# Revit family: ECDFPW314C
name_source: partatom
category: Plumbing Fixtures
units: mm (PartAtom-declared; Revit-internal decimal feet)

## family parameters
Always vertical = Yes
Cut with Voids When Loaded = No
OmniClass Number = 23.45.00.00
OmniClass Title = Sanitary, Laundry, and Cleaning Equipment
Part Type = Normal
Room Calculation Point = No
Round Connector Dimension = Use Diameter
Shared = Yes
Work Plane-Based = No

## types (1)
- ECDFPW314C
    Activation by = Mechanical Front Bubbler Button
    Approx. Shipping Weigh = 26 lbs
    Assembly Code = D2010810
    Bubbler Style = Flexi-Guard ® Safety Bubbler
    CW Connection = Yes
    Chilling Option = Non-refrigerated
    Description = Elkay Slimline Soft Sides Fountain Non-Filtered Non-Refrigerated
Stainless
    Dimensions (L x W x H) = 19-3/4 inch  x 19-3/8 inch  x 20-3/8 inch
    Drain_Furnished = 32 mm  [stored 0.104987 ft]
    Finish = Stainless Steel
    HW Connection = No
    Installation Location = Indoor + Outdoor
    Manufacturer = Elkay
    Model = ECDFPW314C
    Mounting Type = Wall Mount (On Wall)
    No. of Stations Served = 1
    Power = No Electrical Required
    URL = http://www.elkay.com
    Vent Connection = No
    Version = 1.0.0.0
    Waste Connection = Yes
    Waste_outlet = 32 mm  [stored 0.104987 ft]
    Water_Inlet = 10 mm  [stored 0.0328084 ft]

note: [stored X ft] marks values corroborated as IEEE doubles in the binary element streams (Revit-internal decimal feet)

## geometry (parser evidence)
native form markers: Sweep x35
no freeform markers — native parametric forms only
